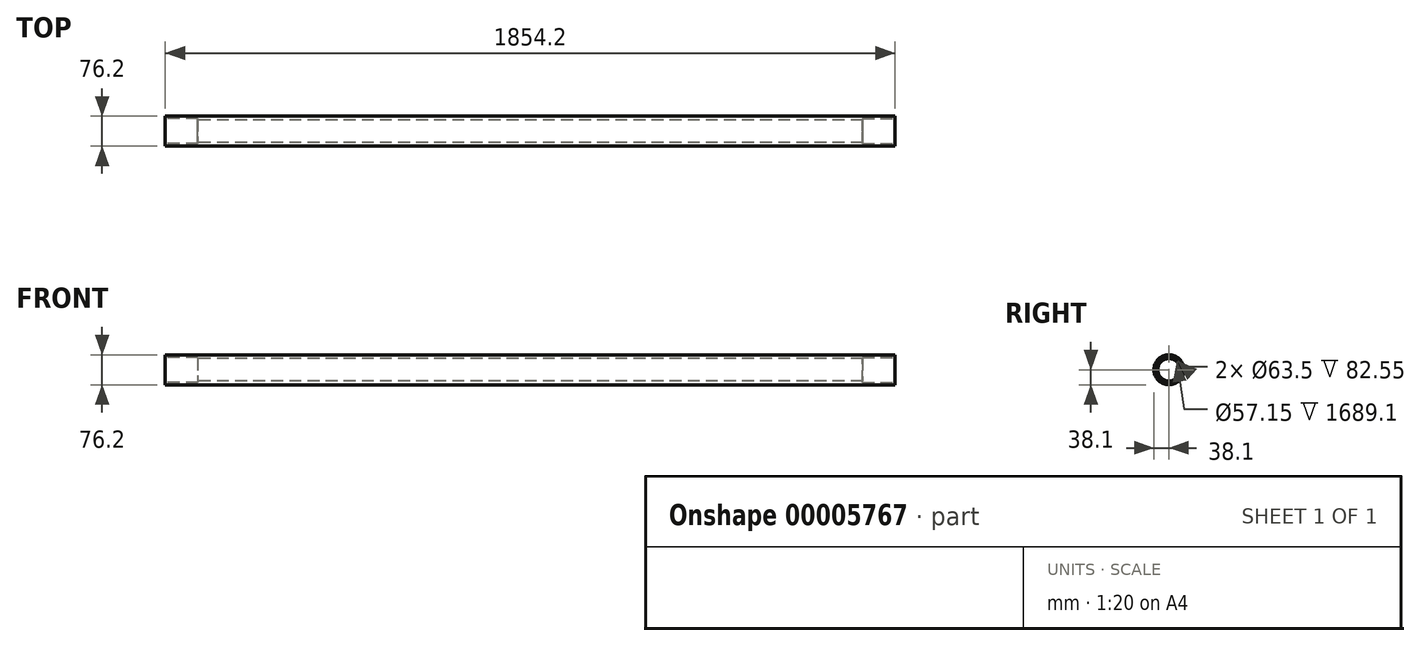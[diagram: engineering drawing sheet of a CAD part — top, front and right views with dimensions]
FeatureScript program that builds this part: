
annotation { "Feature Type Name" : "Feature", "Feature Type Description" : "" }
export const myFeature = defineFeature(function(context is Context, id is Id, definition is map)
    precondition{}
    {
        {
            var Q0;
            Q0=qCreatedBy(makeId("Right.planeOp"),FACE);
            var sketch = newSketch(context, id + "F0", { "sketchPlane" : qUnion([Q0])});
            skCircle(sketch, "E0", {"center": v(0, 0) * mm, "radius": 38.1 * mm});
            skCircle(sketch, "E1", {"center": v(0, 0) * mm, "radius": 28.58 * mm});
            skSolve(sketch);
        }
        {
            var Q0;
            Q0 = qSketchRegion(id + "F0", true);
            extrude(context, id + "F1", {"entities" : qUnion([Q0]), "endBound" : BoundingType.SYMMETRIC, "depth" : 1854.2 * mm});
        }
        {
            var Q0;
            Q0=makeQuery(id+"F1.opExtrude","CAP_FACE",FACE,{"disambiguationData":[OSD([sQuery(id+"F0.wireOp",EDGE,"E0"),sQuery(id+"F0.wireOp",EDGE,"E1")])],"isStart":false});
            var sketch = newSketch(context, id + "F2", { "sketchPlane" : qUnion([Q0])});
            skCircle(sketch, "E2", {"center": v(0, 0) * mm, "radius": 31.75 * mm});
            skSolve(sketch);
        }
        {
            var Q0;
            Q0 = qSketchRegion(id + "F2", true);
            extrude(context, id + "F3", {"entities" : qUnion([Q0]), "operationType" : NewBodyOperationType.REMOVE, "oppositeDirection" : true, "depth" : 82.55 * mm});
        }
        {
            var Q0;
            Q0=makeQuery(id+"F1.opExtrude","CAP_FACE",FACE,{"disambiguationData":[OSD([sQuery(id+"F0.wireOp",EDGE,"E0"),sQuery(id+"F0.wireOp",EDGE,"E1")])],"isStart":true});
            var sketch = newSketch(context, id + "F4", { "sketchPlane" : qUnion([Q0])});
            skCircle(sketch, "E3.0", {"center": v(0, 0) * mm, "radius": 31.75 * mm});
            skSolve(sketch);
        }
        {
            var Q0;
            Q0 = qSketchRegion(id + "F4", true);
            extrude(context, id + "F5", {"entities" : qUnion([Q0]), "operationType" : NewBodyOperationType.REMOVE, "oppositeDirection" : true, "depth" : 82.55 * mm});
        }
    });
